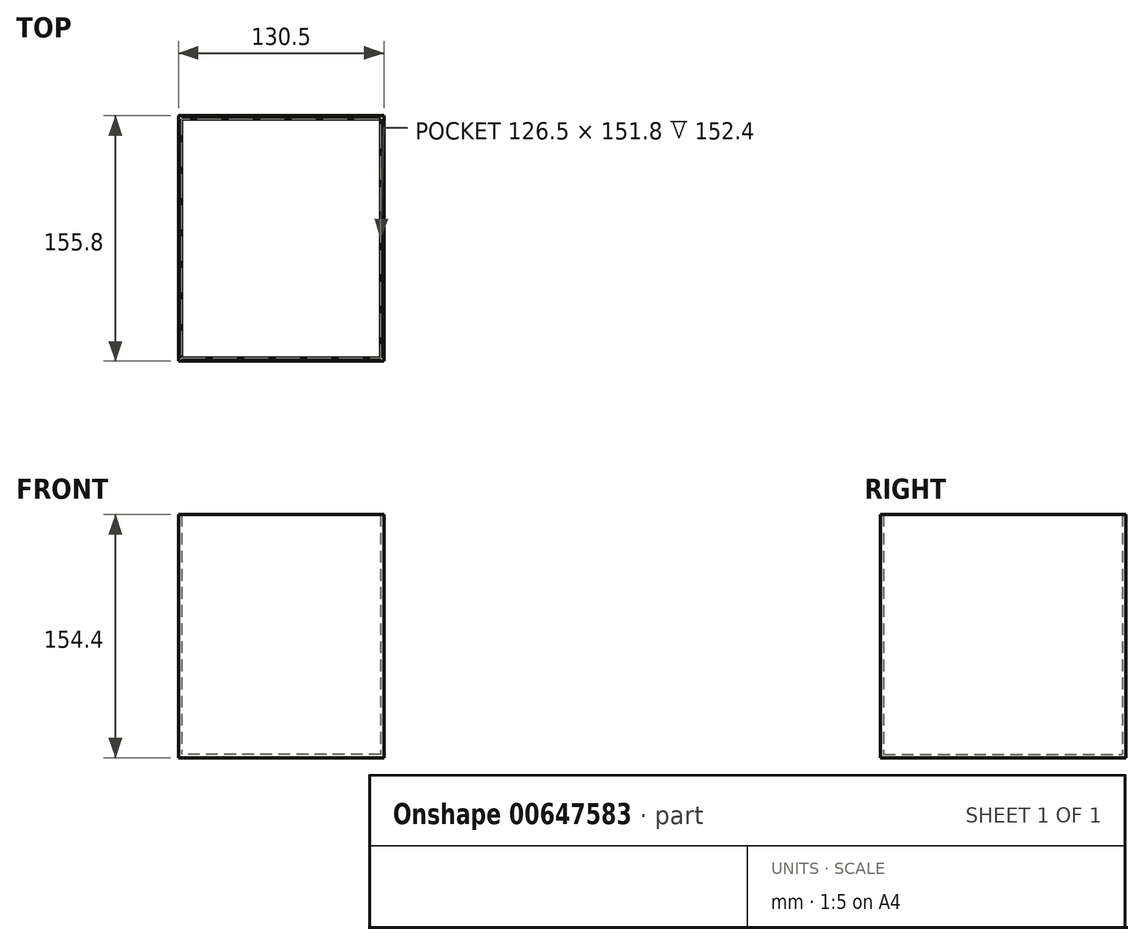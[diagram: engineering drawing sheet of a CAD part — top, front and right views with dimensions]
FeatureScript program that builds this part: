
annotation { "Feature Type Name" : "Feature", "Feature Type Description" : "" }
export const myFeature = defineFeature(function(context is Context, id is Id, definition is map)
    precondition{}
    {
        {
            var Q0;
            Q0=qCreatedBy(makeId("Top.planeOp"),FACE);
            var sketch = newSketch(context, id + "F0", { "sketchPlane" : qUnion([Q0])});
            skLineSegment(sketch, "E0.bottom", {"start": v(63.25, -75.9) * mm, "end": v(-63.25, -75.9) * mm});
            skLineSegment(sketch, "E0.top", {"start": v(63.25, 75.9) * mm, "end": v(-63.25, 75.9) * mm});
            skLineSegment(sketch, "E0.left", {"start": v(63.25, -75.9) * mm, "end": v(63.25, 75.9) * mm});
            skLineSegment(sketch, "E0.right", {"start": v(-63.25, -75.9) * mm, "end": v(-63.25, 75.9) * mm});
            skPoint(sketch, "E0.middle", {"position": v(0, 0) * mm});
            skSolve(sketch);
        }
        {
            var Q0;
            Q0=makeQuery(id+"F0.imprint","IMPRINT",FACE,{"disambiguationData":[TD([[makeQuery(id+"F0.imprint","IMPRINT",EDGE,{"derivedFrom":sQuery(id+"F0.wireOp",EDGE,"E0.bottom")}),-1.0]])]});
            extrude(context, id + "F1", {"entities" : qUnion([Q0]), "depth" : (6 * 25.4) * mm, "offsetDistance" : 25 * mm});
        }
        {
            var Q0;
            Q0=makeQuery(id+"F1.opExtrude","CAP_FACE",FACE,{"disambiguationData":[OSD([sQuery(id+"F0.wireOp",EDGE,"E0.bottom"),sQuery(id+"F0.wireOp",EDGE,"E0.top"),sQuery(id+"F0.wireOp",EDGE,"E0.left"),sQuery(id+"F0.wireOp",EDGE,"E0.right")])],"isStart":false});
            shell(context, id + "F2", {"entities" : qUnion([Q0]), "thickness" : 2 * mm, "oppositeDirection" : true});
        }
    });
